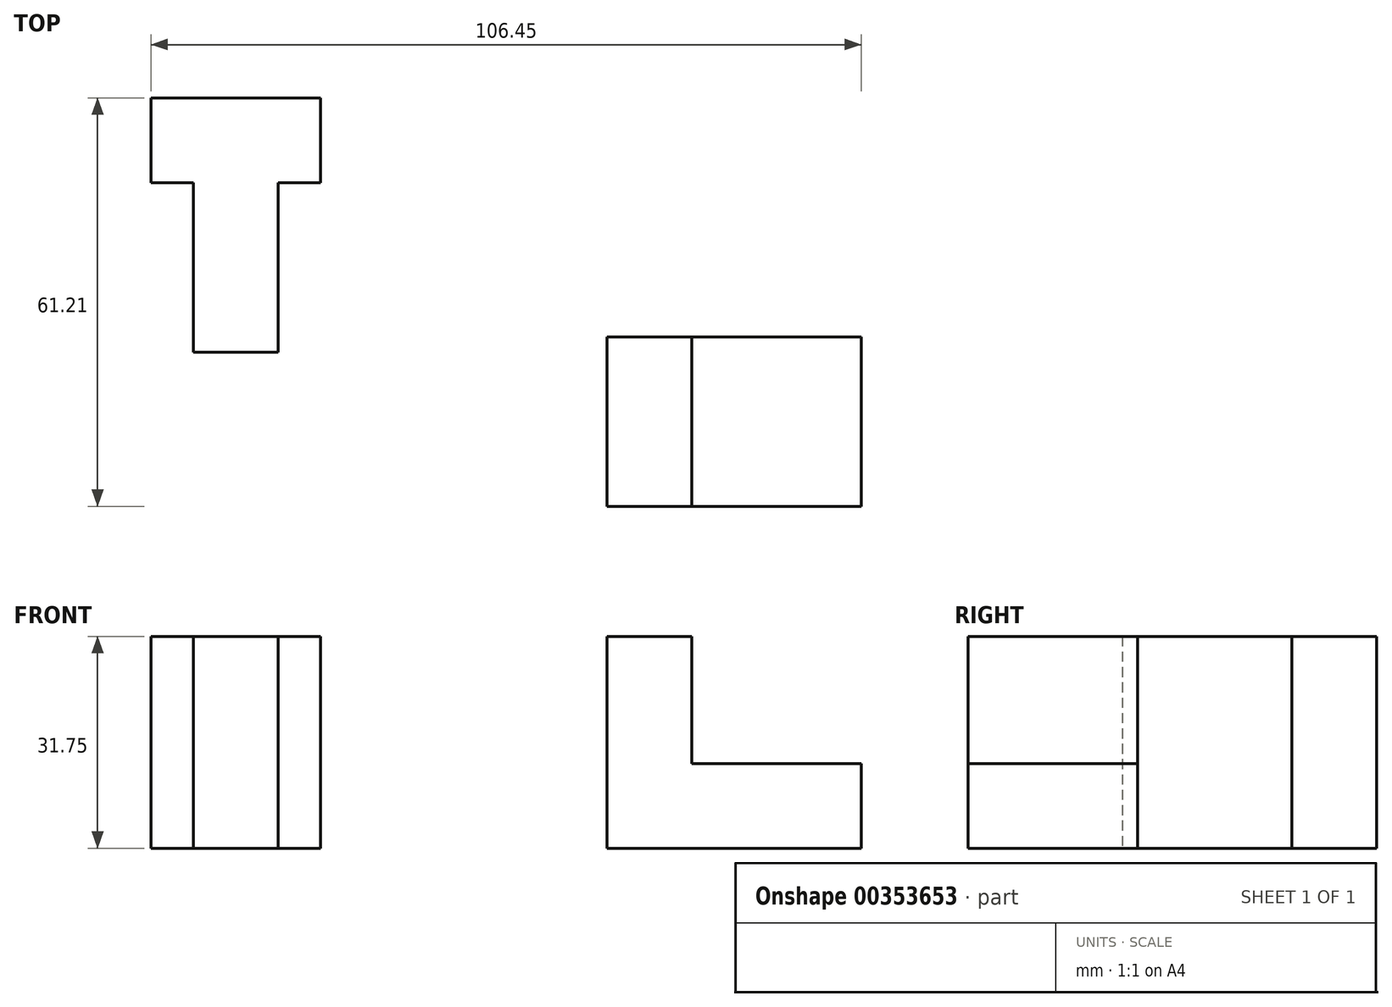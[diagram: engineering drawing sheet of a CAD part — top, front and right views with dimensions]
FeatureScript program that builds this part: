
annotation { "Feature Type Name" : "Feature", "Feature Type Description" : "" }
export const myFeature = defineFeature(function(context is Context, id is Id, definition is map)
    precondition{}
    {
        {
            var Q0;
            Q0=qCreatedBy(makeId("Front.planeOp"),FACE);
            var sketch = newSketch(context, id + "F0", { "sketchPlane" : qUnion([Q0])});
            skLineSegment(sketch, "E0", {"start": v(21.42, 31.75) * mm, "end": v(21.42, 0) * mm});
            skLineSegment(sketch, "E1", {"start": v(21.42, 0) * mm, "end": v(59.52, 0) * mm});
            skLineSegment(sketch, "E2", {"start": v(59.52, 0) * mm, "end": v(59.52, 12.7) * mm});
            skLineSegment(sketch, "E3", {"start": v(59.52, 12.7) * mm, "end": v(34.12, 12.7) * mm});
            skLineSegment(sketch, "E4", {"start": v(34.12, 12.7) * mm, "end": v(34.12, 31.75) * mm});
            skLineSegment(sketch, "E5", {"start": v(34.12, 31.75) * mm, "end": v(21.42, 31.75) * mm});
            skSolve(sketch);
        }
        {
            var Q0;
            Q0 = qSketchRegion(id + "F0", true);
            extrude(context, id + "F1", {"entities" : qUnion([Q0]), "depth" : 25.4 * mm});
        }
        {
            var Q0;
            Q0=qCreatedBy(makeId("Top.planeOp"),FACE);
            var sketch = newSketch(context, id + "F2", { "sketchPlane" : qUnion([Q0])});
            skLineSegment(sketch, "E6", {"start": v(-46.93, 35.81) * mm, "end": v(-46.93, 23.11) * mm});
            skLineSegment(sketch, "E7", {"start": v(-46.93, 23.11) * mm, "end": v(-40.58, 23.11) * mm});
            skLineSegment(sketch, "E8", {"start": v(-40.58, 23.11) * mm, "end": v(-40.58, -2.29) * mm});
            skLineSegment(sketch, "E9", {"start": v(-40.58, -2.29) * mm, "end": v(-27.88, -2.29) * mm});
            skLineSegment(sketch, "E10", {"start": v(-27.88, -2.29) * mm, "end": v(-27.88, 23.11) * mm});
            skLineSegment(sketch, "E11", {"start": v(-27.88, 23.11) * mm, "end": v(-21.53, 23.11) * mm});
            skLineSegment(sketch, "E12", {"start": v(-21.53, 23.11) * mm, "end": v(-21.53, 35.81) * mm});
            skLineSegment(sketch, "E13", {"start": v(-21.53, 35.81) * mm, "end": v(-46.93, 35.81) * mm});
            skSolve(sketch);
        }
        {
            var Q0;
            Q0=makeQuery(id+"F2.imprint","IMPRINT",FACE,{"disambiguationData":[TD([[makeQuery(id+"F2.imprint","IMPRINT",EDGE,{"derivedFrom":sQuery(id+"F2.wireOp",EDGE,"E6")}),1.0]])]});
            extrude(context, id + "F3", {"entities" : qUnion([Q0]), "depth" : 31.75 * mm});
        }
    });
